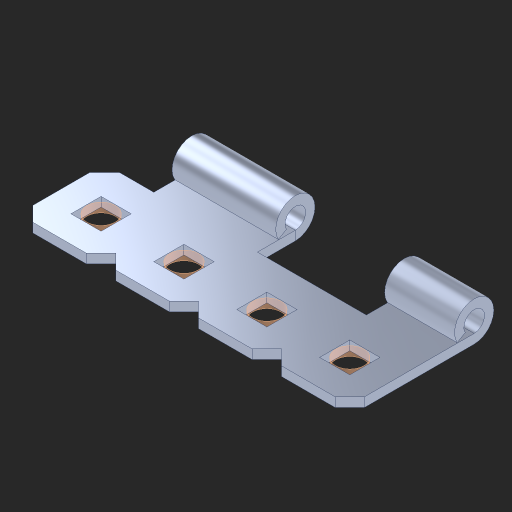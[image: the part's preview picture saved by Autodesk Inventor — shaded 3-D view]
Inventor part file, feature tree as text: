
AUTODESK INVENTOR PART (.ipt)
format: ipt  version: 2023 (Build 270158000, 158)  size: 215,552 bytes
history: native  units: in
note: dims shown in document units (in); Inventor stores cm internally (conversion verified against a paired STEP export)
features: other x6, extrude x5, sketch x2, pattern_linear x1, imported_body x1
ambient origin geometry x8: Origin, YZ Plane, XZ Plane, XY Plane, X Axis, Y Axis, Z Axis, Center Point
bodies: Body1 (feature_tree), Body2 (feature_tree), Body3 (feature_tree), Body4 (feature_tree), Body5 (feature_tree)
feature tree (15):
  other  "Cut-Extrude3"
  other  "Bottom"
  pattern_linear  "Rectangular Pattern1"  Spacing1=0.5in  [1 undecoded]
  extrude  "Extrusion1"  Depth=0.5in
  imported_body  "Base1"
  sketch  "Sketch1"  dims[d15=0.046in d16=0.0in]
  other  "Srf1"
  other  "Srf2"
  other  "Srf3"
  other  "Srf4"
  sketch  "Sketch4"  dims[d19=0.5in d30=0.5in d31=0.0in d32=0.172in]
  extrude  "ExtrusionSrf1"  [1 undecoded]
  extrude  "ExtrusionSrf2"  [1 undecoded]
  extrude  "ExtrusionSrf3"  [1 undecoded]
  extrude  "ExtrusionSrf4"  [1 undecoded]
note: 5 required parameter values undecoded (feature->parameter linkage not recoverable at this tier; creation-order binding heuristic only, values carry confidence <= 0.55)
